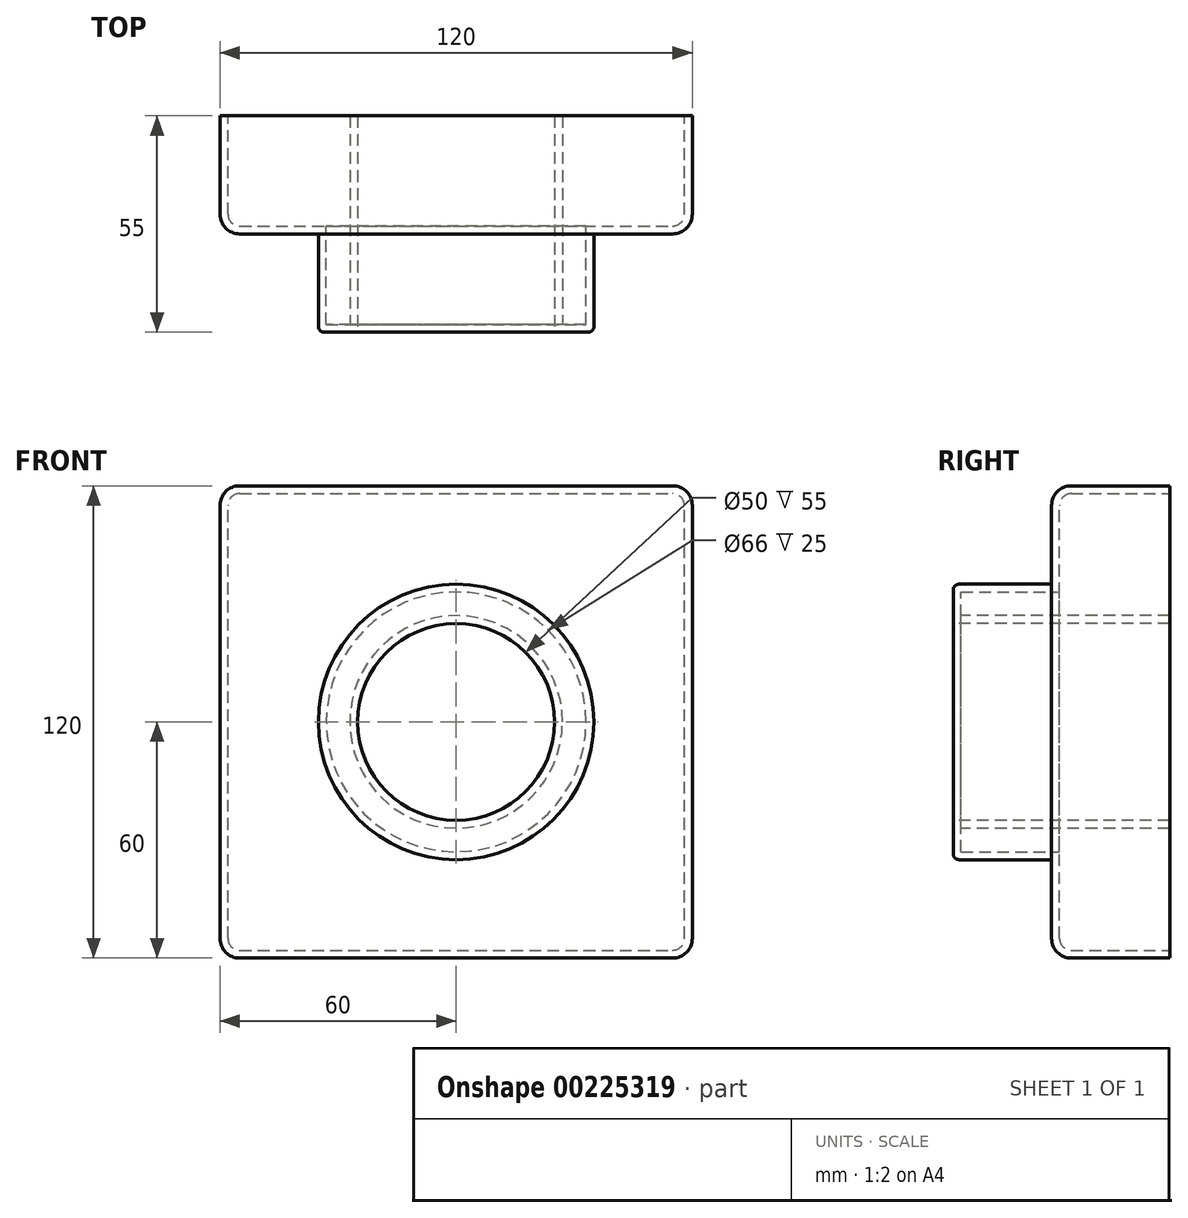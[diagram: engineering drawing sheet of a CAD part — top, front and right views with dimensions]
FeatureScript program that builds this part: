
annotation { "Feature Type Name" : "Feature", "Feature Type Description" : "" }
export const myFeature = defineFeature(function(context is Context, id is Id, definition is map)
    precondition{}
    {
        {
            var Q0;
            Q0=qCreatedBy(makeId("Front.planeOp"),FACE);
            var sketch = newSketch(context, id + "F0", { "sketchPlane" : qUnion([Q0])});
            skLineSegment(sketch, "E0.bottom", {"start": v(0, 0) * mm, "end": v(120, 0) * mm});
            skLineSegment(sketch, "E0.top", {"start": v(0, 120) * mm, "end": v(120, 120) * mm});
            skLineSegment(sketch, "E0.left", {"start": v(0, 0) * mm, "end": v(0, 120) * mm});
            skLineSegment(sketch, "E0.right", {"start": v(120, 0) * mm, "end": v(120, 120) * mm});
            skSolve(sketch);
        }
        {
            var Q0;
            Q0 = qSketchRegion(id + "F0", true);
            extrude(context, id + "F1", {"entities" : qUnion([Q0]), "depth" : 30 * mm});
        }
        {
            var Q0;
            Q0=makeQuery(id+"F1.opExtrude","CAP_FACE",FACE,{"disambiguationData":[OSD([sQuery(id+"F0.wireOp",EDGE,"E0.bottom"),sQuery(id+"F0.wireOp",EDGE,"E0.top"),sQuery(id+"F0.wireOp",EDGE,"E0.left"),sQuery(id+"F0.wireOp",EDGE,"E0.right")])],"isStart":false});
            var sketch = newSketch(context, id + "F2", { "sketchPlane" : qUnion([Q0])});
            skCircle(sketch, "E1", {"center": v(60, 60) * mm, "radius": 35 * mm});
            skSolve(sketch);
        }
        {
            var Q0;
            Q0 = qSketchRegion(id + "F2", true);
            extrude(context, id + "F3", {"entities" : qUnion([Q0]), "operationType" : NewBodyOperationType.ADD, "depth" : 25 * mm});
        }
        {
            var Q0;
            Q0=makeQuery(id+"F3.opExtrude","CAP_FACE",FACE,{"disambiguationData":[OSD([sQuery(id+"F2.wireOp",EDGE,"E1")])],"isStart":false});
            var sketch = newSketch(context, id + "F4", { "sketchPlane" : qUnion([Q0])});
            skCircle(sketch, "E2", {"center": v(60, 60) * mm, "radius": 25 * mm});
            skSolve(sketch);
        }
        {
            var Q0;
            Q0 = qSketchRegion(id + "F4", true);
            extrude(context, id + "F5", {"entities" : qUnion([Q0]), "operationType" : NewBodyOperationType.REMOVE, "endBound" : BoundingType.THROUGH_ALL, "oppositeDirection" : true, "depth" : 25 * mm});
        }
        {
            var Q0;
            Q0=makeQuery(id+"F5.boolean.opBoolean","COPY",EDGE,{"derivedFrom":makeQuery(id+"F5.opExtrude","CAP_EDGE",EDGE,{"disambiguationData":[OSD([sQuery(id+"F4.wireOp",EDGE,"E2")])],"isStart":true})});
            var Q1;
            Q1=makeQuery(id+"F3.opExtrude","CAP_EDGE",EDGE,{"disambiguationData":[OSD([sQuery(id+"F2.wireOp",EDGE,"E1")])],"isStart":false});
            fillet(context, id + "F6", {"entities" : qUnion([Q0, Q1]), "radius" : 1.5 * mm, "tangentPropagation" : true, "allowEdgeOverflow" : false});
        }
        {
            var Q0;
            Q0=makeQuery(id+"F3.opExtrude","CAP_EDGE",EDGE,{"disambiguationData":[OSD([sQuery(id+"F2.wireOp",EDGE,"E1")])],"isStart":true});
            var Q1;
            Q1=makeQuery(id+"F1.opExtrude","SWEPT_EDGE",EDGE,{"disambiguationData":[OSD([sQuery(id+"F0.wireOp",EDGE,"E0.top"),sQuery(id+"F0.wireOp",EDGE,"E0.right")])]});
            var Q2;
            Q2=makeQuery(id+"F1.opExtrude","CAP_EDGE",EDGE,{"disambiguationData":[OSD([sQuery(id+"F0.wireOp",EDGE,"E0.right")])],"isStart":false});
            var Q3;
            Q3=makeQuery(id+"F1.opExtrude","CAP_EDGE",EDGE,{"disambiguationData":[OSD([sQuery(id+"F0.wireOp",EDGE,"E0.top")])],"isStart":false});
            var Q4;
            Q4=makeQuery(id+"F1.opExtrude","SWEPT_EDGE",EDGE,{"disambiguationData":[OSD([sQuery(id+"F0.wireOp",EDGE,"E0.top"),sQuery(id+"F0.wireOp",EDGE,"E0.left")])]});
            var Q5;
            Q5=makeQuery(id+"F1.opExtrude","SWEPT_EDGE",EDGE,{"disambiguationData":[OSD([sQuery(id+"F0.wireOp",EDGE,"E0.bottom"),sQuery(id+"F0.wireOp",EDGE,"E0.right")])]});
            var Q6;
            Q6=makeQuery(id+"F1.opExtrude","CAP_EDGE",EDGE,{"disambiguationData":[OSD([sQuery(id+"F0.wireOp",EDGE,"E0.bottom")])],"isStart":false});
            var Q7;
            Q7=makeQuery(id+"F1.opExtrude","SWEPT_EDGE",EDGE,{"disambiguationData":[OSD([sQuery(id+"F0.wireOp",EDGE,"E0.bottom"),sQuery(id+"F0.wireOp",EDGE,"E0.left")])]});
            var Q8;
            Q8=makeQuery(id+"F1.opExtrude","CAP_EDGE",EDGE,{"disambiguationData":[OSD([sQuery(id+"F0.wireOp",EDGE,"E0.left")])],"isStart":false});
            fillet(context, id + "F7", {"entities" : qUnion([Q0, Q1, Q2, Q3, Q4, Q5, Q6, Q7, Q8]), "radius" : 5 * mm, "tangentPropagation" : true, "allowEdgeOverflow" : false});
        }
        {
            var Q0;
            Q0=makeQuery(id+"F1.opExtrude","CAP_FACE",FACE,{"disambiguationData":[OSD([sQuery(id+"F0.wireOp",EDGE,"E0.bottom"),sQuery(id+"F0.wireOp",EDGE,"E0.top"),sQuery(id+"F0.wireOp",EDGE,"E0.left"),sQuery(id+"F0.wireOp",EDGE,"E0.right")])],"isStart":true});
            shell(context, id + "F8", {"entities" : qUnion([Q0]), "thickness" : 2 * mm});
        }
    });
